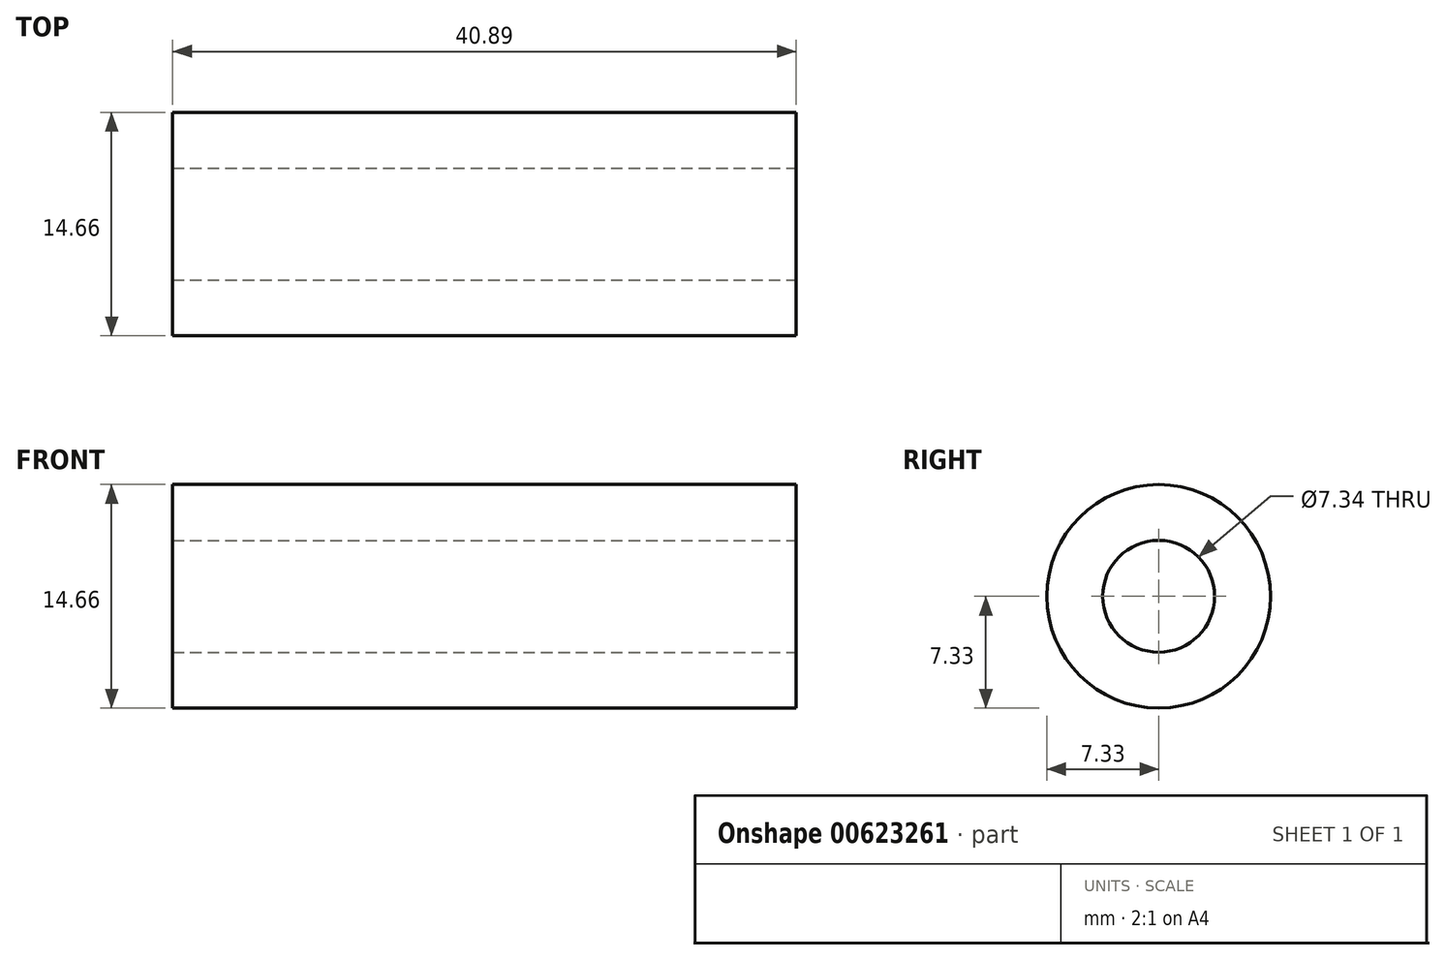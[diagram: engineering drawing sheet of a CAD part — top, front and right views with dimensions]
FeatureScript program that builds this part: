
annotation { "Feature Type Name" : "Feature", "Feature Type Description" : "" }
export const myFeature = defineFeature(function(context is Context, id is Id, definition is map)
    precondition{}
    {
        {
            var Q0;
            Q0=qCreatedBy(makeId("Right.planeOp"),FACE);
            var sketch = newSketch(context, id + "F0", { "sketchPlane" : qUnion([Q0])});
            skCircle(sketch, "E0", {"center": v(0, 0) * mm, "radius": 7.33 * mm});
            skSolve(sketch);
        }
        {
            var Q0;
            Q0 = qSketchRegion(id + "F0", true);
            var Q1;
            Q1 = qSketchRegion(id + "F2", true);
            extrude(context, id + "F1", {"entities" : qUnion([Q0, Q1]), "oppositeDirection" : true, "depth" : 40.9 * mm, "offsetDistance" : 25.4 * mm});
        }
        {
            var Q0;
            Q0=qCreatedBy(makeId("Right.planeOp"),FACE);
            var sketch = newSketch(context, id + "F2", { "sketchPlane" : qUnion([Q0])});
            skCircle(sketch, "E1", {"center": v(0, 0) * mm, "radius": 3.67 * mm});
            skSolve(sketch);
        }
        {
            var Q0;
            Q0 = qSketchRegion(id + "F2", true);
            extrude(context, id + "F3", {"entities" : qUnion([Q0]), "operationType" : NewBodyOperationType.REMOVE, "oppositeDirection" : true, "depth" : 81.53 * mm, "offsetDistance" : 25.4 * mm});
        }
    });
